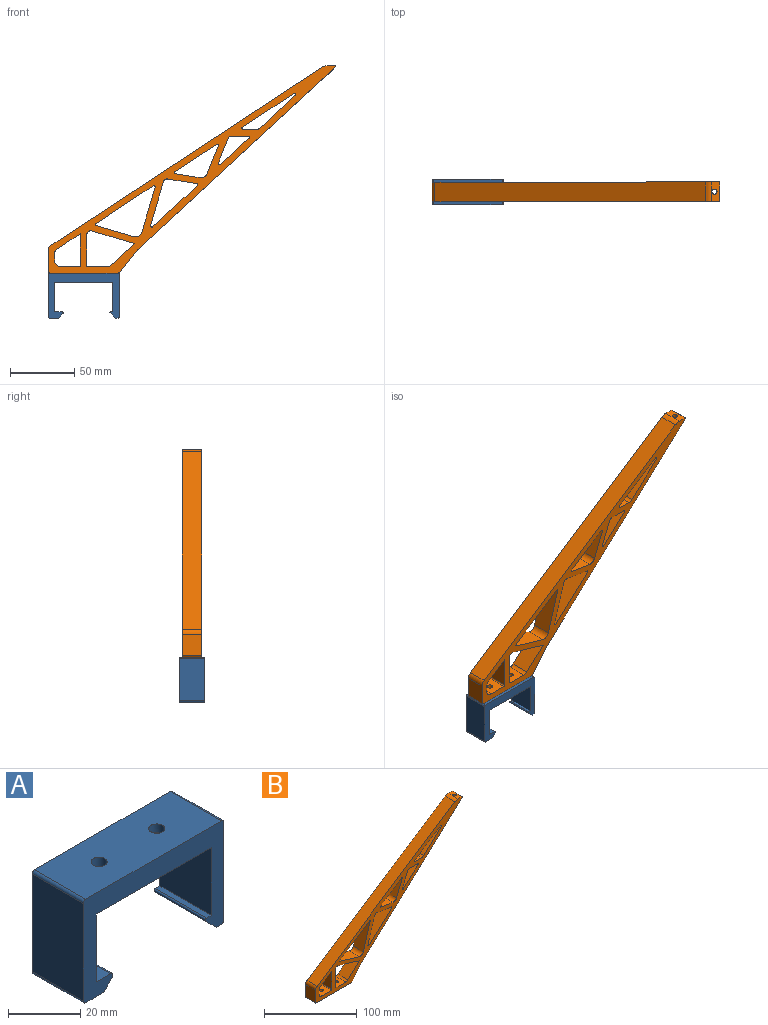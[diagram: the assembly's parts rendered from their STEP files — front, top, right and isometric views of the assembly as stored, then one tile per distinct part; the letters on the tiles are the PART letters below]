
ASSEMBLY  parts=2 mates=1
PART A: 26 faces, bbox 55x20x35 mm
  f0: plane 20x3.29mm, normal (0.71,0,-0.71), area 93.1mm2, adj f11,f12,f13,f14
  f1: plane 20x5.59mm, normal (0,0,1), area 111.7mm2, adj f2,f12,f13,f14
  f2: plane 23x20mm, normal (1,0,0), area 460mm2, adj f1,f3,f12,f13
  f3: plane 45x20mm, normal (0,0,-1), area 793.1mm2, adj f2,f4,f12,f13,f22,f25
  f4: plane 23x20mm, normal (-1,0,0), area 460mm2, adj f3,f5,f12,f13
  f5: plane 20x1.79mm, normal (0,0,1), area 35.9mm2, adj f4,f12,f13,f15
  f6: plane 20x4.15mm, normal (-0.71,0,-0.71), area 117.3mm2, adj f7,f12,f13,f15
  f7: plane 20x2mm, normal (0,0,-1), area 40mm2, adj f6,f12,f13,f16
  f8: plane 33x20mm, normal (1,0,0), area 660mm2, adj f12,f13,f16,f17
  f9: plane 53x20mm, normal (0,0,1), area 1028.2mm2, adj f12,f13,f17,f18,f20,f23
  f10: plane 33x20mm, normal (-1,0,0), area 660mm2, adj f12,f13,f18,f19
  f11: plane 20x7mm, normal (0,0,-1), area 140mm2, adj f0,f12,f13,f19
  f12: plane 55x35mm, normal (0,-1,0), area 692.6mm2, adj f0,f1,f2,f3,f4,f5,f6,f7
  f13: plane 55x35mm, normal (0,1,0), area 692.6mm2, adj f0,f1,f2,f3,f4,f5,f6,f7
  f14: cylinder r=1mm len=20mm, axis (0,1,0), area 47.1mm2, adj f0,f1,f12,f13
  f15: cylinder r=0.5mm len=20mm, axis (0,1,0), area 23.6mm2, adj f5,f6,f12,f13
  f16: cylinder r=1mm len=20mm, axis (0,1,0), area 31.4mm2, adj f7,f8,f12,f13
  f17: cylinder r=1mm len=20mm, axis (0,1,0), area 31.4mm2, adj f8,f9,f12,f13
  f18: cylinder r=1mm len=20mm, axis (0,-1,0), area 31.4mm2, adj f9,f10,f12,f13
  f19: cylinder r=1mm len=20mm, axis (0,1,0), area 31.4mm2, adj f10,f11,f12,f13
  f20: cylinder r=2.25mm len=4.5mm, axis (0,0,-1), area 42.4mm2, adj f9,f21
  f21: plane 8.25x8.25mm, normal (0,0,-1), area 37.6mm2, adj f20,f22
  f22: cylinder r=4.12mm len=8.25mm, axis (0,0,-1), area 103.7mm2, adj f3,f21
  f23: cylinder r=2.25mm len=4.5mm, axis (0,0,-1), area 42.4mm2, adj f9,f24
  f24: plane 8.25x8.25mm, normal (0,0,-1), area 37.6mm2, adj f23,f25
  f25: cylinder r=4.12mm len=8.25mm, axis (0,0,-1), area 103.7mm2, adj f3,f24
PART B: 61 faces, bbox 223.2x15x160.7 mm
  f0: plane 24.45x15mm, normal (-1,0,0), area 366.8mm2, adj f28,f29,f30,f50
  f1: plane 15x14mm, normal (0,0,1), area 194.1mm2, adj f29,f30,f33,f38,f50
  f2: plane 15x4.61mm, normal (1,0,0), area 69.1mm2, adj f29,f30,f36,f38
  f3: plane 15x9.75mm, normal (0,0,1), area 146.3mm2, adj f29,f30,f41,f55
  f4: plane 39.51x25.97mm, normal (0.55,0,-0.84), area 709.2mm2, adj f29,f30,f55,f56
  f5: plane 19.12x15mm, normal (0.93,0,-0.37), area 308.8mm2, adj f29,f30,f45,f58
  f6: plane 15x12.63mm, normal (0,0,-1), area 189.4mm2, adj f29,f30,f45,f57
  f7: plane 18.89x15mm, normal (0.16,0,0.99), area 286.9mm2, adj f29,f30,f42,f53
  f8: plane 31.81x20.91mm, normal (0.55,0,-0.84), area 571mm2, adj f29,f30,f53,f54
  f9: plane 15x14.67mm, normal (0,0,1), area 204.1mm2, adj f29,f30,f32,f40,f49
  f10: plane 23.73x15mm, normal (1,0,0), area 355.9mm2, adj f29,f30,f43,f49
  f11: plane 33.14x15mm, normal (-0.28,0,-0.96), area 518.2mm2, adj f24,f29,f30,f43
  f12: plane 34.88x15mm, normal (-0.96,0,0.28), area 545.5mm2, adj f29,f30,f39,f52
  f13: plane 28.94x15mm, normal (0.28,0,0.96), area 452.5mm2, adj f29,f30,f39,f51
  f14: plane 34.5x31.79mm, normal (-0.68,0,0.74), area 703.7mm2, adj f29,f30,f48,f59
  f15: plane 33.95x15mm, normal (0.96,0,-0.28), area 530.9mm2, adj f29,f30,f44,f48
  f16: plane 53.52x15mm, normal (0,0,-1), area 770.9mm2, adj f29,f30,f32,f33,f46,f60
  f17: plane 18.13x15mm, normal (0.78,0,-0.62), area 347mm2, adj f29,f30,f46,f47
  f18: plane 153.29x141.21mm, normal (0.68,0,-0.74), area 3109.2mm2, adj f29,f30,f31,f34,f47
  f19: plane 15x6.33mm, normal (0,0,1), area 82.3mm2, adj f29,f30,f31,f34,f35
  f20: plane 209.76x137.9mm, normal (-0.55,0,0.84), area 3765.4mm2, adj f29,f30,f35,f37
  f21: plane 27.05x24.92mm, normal (-0.68,0,0.74), area 551.6mm2, adj f29,f30,f41,f56
  f22: plane 22.12x20.38mm, normal (-0.68,0,0.74), area 451.2mm2, adj f29,f30,f57,f58
  f23: plane 21.48x15mm, normal (-0.93,0,0.37), area 346.9mm2, adj f29,f30,f42,f54
  f24: plane 17.93x16.52mm, normal (-0.68,0,0.74), area 365.7mm2, adj f11,f29,f30,f40
  f25: plane 44.19x29.06mm, normal (0.55,0,-0.84), area 793.3mm2, adj f29,f30,f51,f52
  f26: plane 22.25x15mm, normal (-0.16,0,-0.99), area 338mm2, adj f29,f30,f44,f59
  f27: plane 16.3x15mm, normal (-1,0,0), area 244.6mm2, adj f29,f30,f37,f60
  f28: plane 17.75x15mm, normal (0.55,0,-0.84), area 318.6mm2, adj f0,f29,f30,f36
  f29: plane 223.23x160.7mm, normal (0,-1,0), area 3715.8mm2, adj f0,f1,f2,f3,f4,f5,f6,f7
  f30: plane 223.23x160.7mm, normal (0,1,0), area 3715.8mm2, adj f0,f1,f2,f3,f4,f5,f6,f7
  f31: cylinder r=2mm len=6.47mm, axis (0,0,1), area 57.9mm2, adj f18,f19
  f32: cylinder r=2.25mm len=5mm, axis (0,0,-1), area 70.7mm2, adj f9,f16
  f33: cylinder r=2.25mm len=5mm, axis (0,0,-1), area 70.7mm2, adj f1,f16
  f34: cylinder r=0.5mm len=15mm, axis (0,-1,0), area 18mm2, adj f18,f19,f29,f30
  f35: cylinder r=8mm len=15mm, axis (0,1,0), area 69.8mm2, adj f19,f20,f29,f30
  f36: cylinder r=5mm len=15mm, axis (0,-1,0), area 74.2mm2, adj f2,f28,f29,f30
  f37: cylinder r=5mm len=15mm, axis (0,1,0), area 74.2mm2, adj f20,f27,f29,f30
  f38: cylinder r=5mm len=15mm, axis (0,1,0), area 117.8mm2, adj f1,f2,f29,f30
  f39: cylinder r=5mm len=15mm, axis (0,1,0), area 117.8mm2, adj f12,f13,f29,f30
  f40: cylinder r=5mm len=15mm, axis (0,-1,0), area 55.8mm2, adj f9,f24,f29,f30
  f41: cylinder r=5mm len=15mm, axis (0,1,0), area 55.8mm2, adj f3,f21,f29,f30
  f42: cylinder r=5mm len=15mm, axis (0,1,0), area 101.2mm2, adj f7,f23,f29,f30
  f43: cylinder r=3mm len=15mm, axis (0,-1,0), area 83.6mm2, adj f10,f11,f29,f30
  f44: cylinder r=3mm len=15mm, axis (0,-1,0), area 64.9mm2, adj f15,f26,f29,f30
  f45: cylinder r=3mm len=15mm, axis (0,1,0), area 53.6mm2, adj f5,f6,f29,f30
  f46: cylinder r=1mm len=15mm, axis (0,1,0), area 13.5mm2, adj f16,f17,f29,f30
  f47: cylinder r=1mm len=15mm, axis (0,-1,0), area 2.3mm2, adj f17,f18,f29,f30
  f48: cylinder r=1mm len=15mm, axis (0,1,0), area 39mm2, adj f14,f15,f29,f30
  f49: cylinder r=1mm len=15mm, axis (0,1,0), area 23.6mm2, adj f9,f10,f29,f30
  f50: cylinder r=1mm len=15mm, axis (0,-1,0), area 23.6mm2, adj f0,f1,f29,f30
  f51: cylinder r=1mm len=15mm, axis (0,-1,0), area 34.1mm2, adj f13,f25,f29,f30
  f52: cylinder r=1mm len=15mm, axis (0,1,0), area 36.6mm2, adj f12,f25,f29,f30
  f53: cylinder r=1mm len=15mm, axis (0,-1,0), area 36mm2, adj f7,f8,f29,f30
  f54: cylinder r=1mm len=15mm, axis (0,1,0), area 38mm2, adj f8,f23,f29,f30
  f55: cylinder r=1mm len=15mm, axis (0,-1,0), area 38.4mm2, adj f3,f4,f29,f30
  f56: cylinder r=1mm len=15mm, axis (0,1,0), area 44.7mm2, adj f4,f21,f29,f30
  f57: cylinder r=1mm len=15mm, axis (0,1,0), area 36mm2, adj f6,f22,f29,f30
  f58: cylinder r=1mm len=15mm, axis (0,-1,0), area 40.4mm2, adj f5,f22,f29,f30
  f59: cylinder r=1mm len=15mm, axis (0,1,0), area 33.6mm2, adj f14,f26,f29,f30
  f60: cylinder r=1mm len=15mm, axis (0,-1,0), area 23.6mm2, adj f16,f27,f29,f30
PLACE A at identity fixed
PLACE B t=(-0.27,-2.5,7)mm
MATE fastened B.f16 <-> A.f9  axis (0,0,-1) through (0,-10,7)mm
